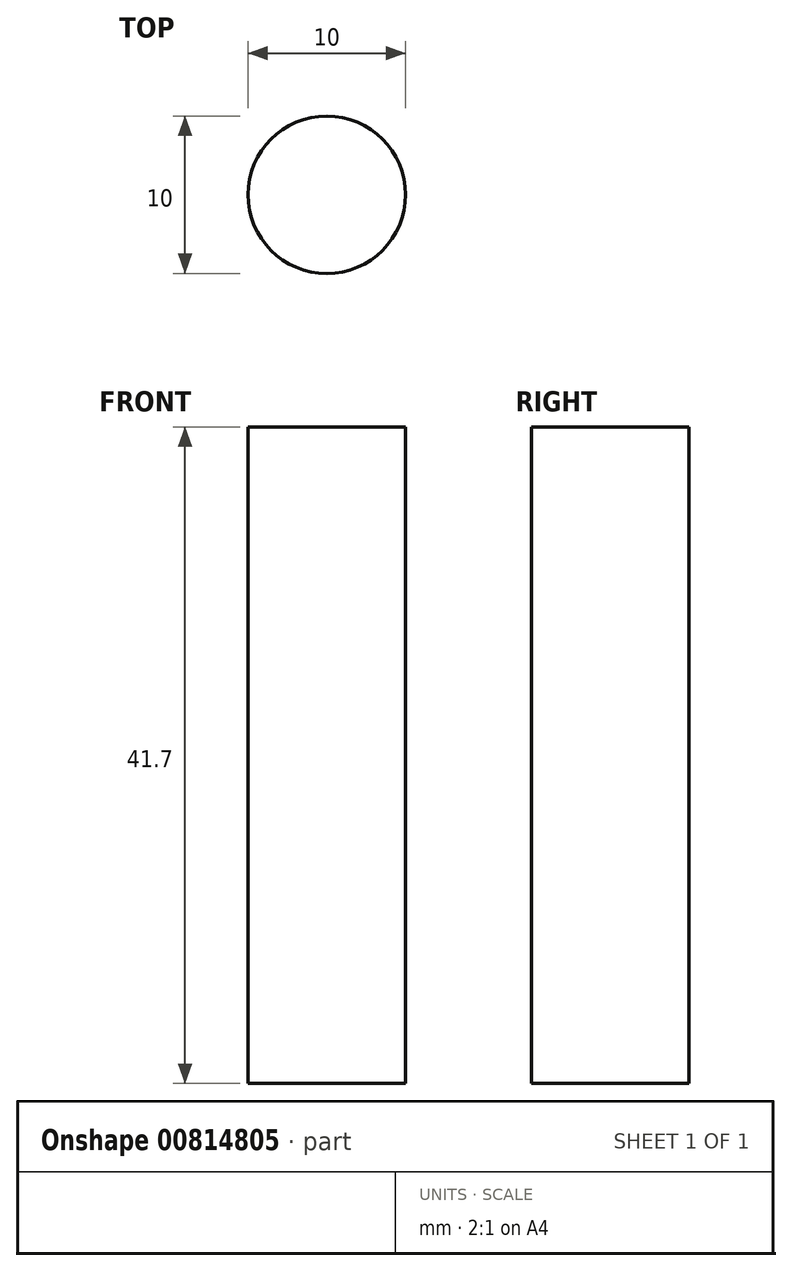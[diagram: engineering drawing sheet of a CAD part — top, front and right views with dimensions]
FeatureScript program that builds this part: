
annotation { "Feature Type Name" : "Feature", "Feature Type Description" : "" }
export const myFeature = defineFeature(function(context is Context, id is Id, definition is map)
    precondition{}
    {
        {
            var Q0;
            Q0=qCreatedBy(makeId("Top.planeOp"),FACE);
            var sketch = newSketch(context, id + "F0", { "sketchPlane" : qUnion([Q0])});
            skCircle(sketch, "E0", {"center": v(0, 0) * mm, "radius": 5 * mm});
            skSolve(sketch);
        }
        {
            var Q0;
            Q0=makeQuery(id+"F0.imprint","IMPRINT",FACE,{"disambiguationData":[TD([[makeQuery(id+"F0.imprint","IMPRINT",EDGE,{"derivedFrom":sQuery(id+"F0.wireOp",EDGE,"E0")}),1.0]])]});
            extrude(context, id + "F1", {"entities" : qUnion([Q0]), "depth" : 41.7 * mm, "offsetDistance" : 25 * mm});
        }
    });
